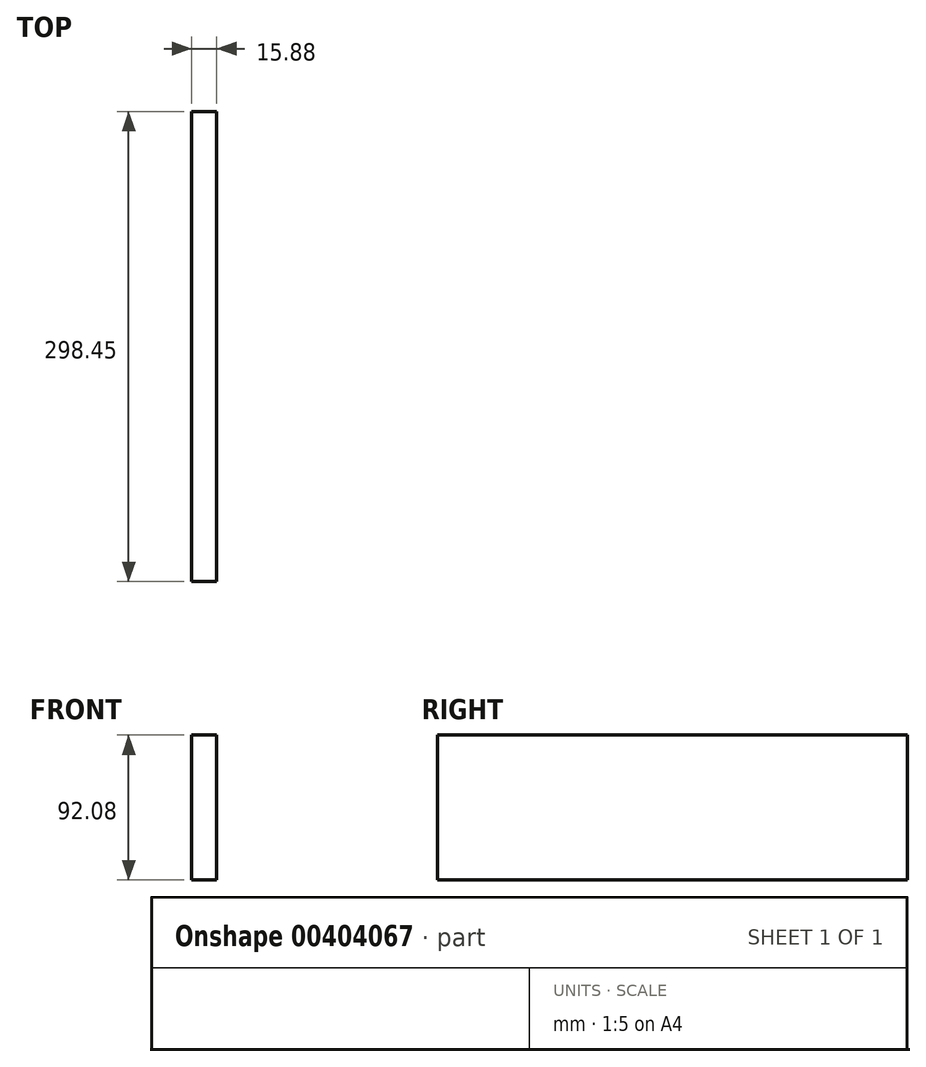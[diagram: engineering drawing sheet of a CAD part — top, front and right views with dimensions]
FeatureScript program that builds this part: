
annotation { "Feature Type Name" : "Feature", "Feature Type Description" : "" }
export const myFeature = defineFeature(function(context is Context, id is Id, definition is map)
    precondition{}
    {
        {
            var Q0;
            Q0=qCreatedBy(makeId("Right.planeOp"),FACE);
            var sketch = newSketch(context, id + "F0", { "sketchPlane" : qUnion([Q0])});
            skLineSegment(sketch, "E0.bottom", {"start": v(-109.66, 54.85) * mm, "end": v(188.8, 54.85) * mm});
            skLineSegment(sketch, "E0.top", {"start": v(-109.66, -37.23) * mm, "end": v(188.8, -37.23) * mm});
            skLineSegment(sketch, "E0.left", {"start": v(-109.66, 54.85) * mm, "end": v(-109.66, -37.23) * mm});
            skLineSegment(sketch, "E0.right", {"start": v(188.8, 54.85) * mm, "end": v(188.8, -37.23) * mm});
            skSolve(sketch);
        }
        {
            var Q0;
            Q0=makeQuery(id+"F0.imprint","IMPRINT",FACE,{"disambiguationData":[TD([[makeQuery(id+"F0.imprint","IMPRINT",EDGE,{"derivedFrom":sQuery(id+"F0.wireOp",EDGE,"E0.bottom")}),-1.0]])]});
            extrude(context, id + "F1", {"entities" : qUnion([Q0]), "depth" : 15.88 * mm});
        }
    });
